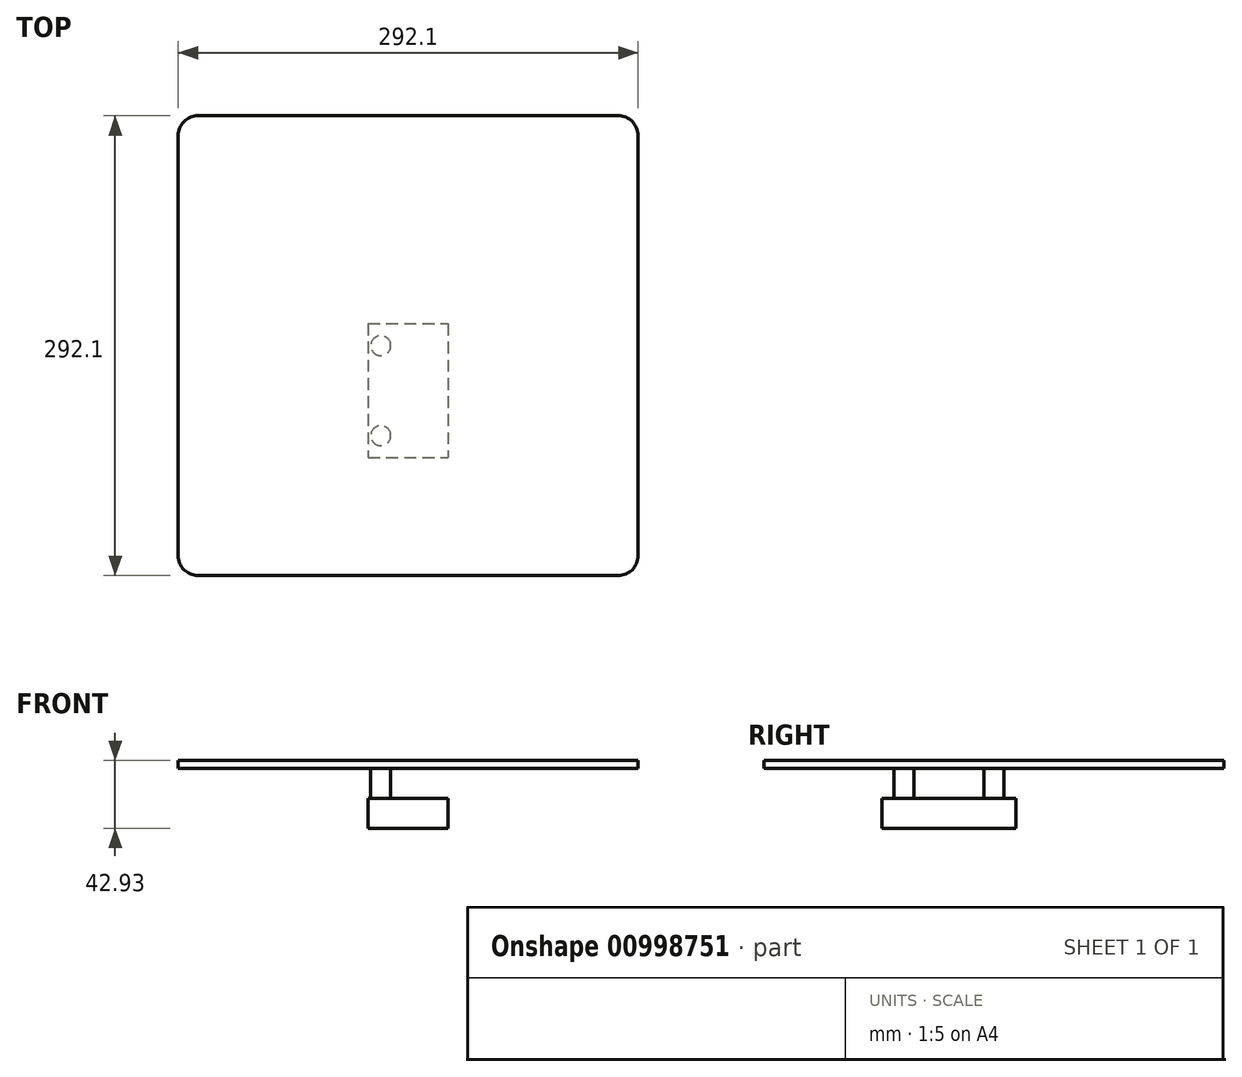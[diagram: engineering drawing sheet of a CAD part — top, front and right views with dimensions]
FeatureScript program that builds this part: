
annotation { "Feature Type Name" : "Feature", "Feature Type Description" : "" }
export const myFeature = defineFeature(function(context is Context, id is Id, definition is map)
    precondition{}
    {
        {
            var Q0;
            Q0=qCreatedBy(makeId("Top.planeOp"),FACE);
            var sketch = newSketch(context, id + "F0", { "sketchPlane" : qUnion([Q0])});
            skLineSegment(sketch, "E0.bottom", {"start": v(133.35, 146.05) * mm, "end": v(-133.35, 146.05) * mm});
            skLineSegment(sketch, "E0.top", {"start": v(133.35, -146.05) * mm, "end": v(-133.35, -146.05) * mm});
            skLineSegment(sketch, "E0.left", {"start": v(146.05, 133.35) * mm, "end": v(146.05, -133.35) * mm});
            skLineSegment(sketch, "E0.right", {"start": v(-146.05, 133.35) * mm, "end": v(-146.05, -133.35) * mm});
            skPoint(sketch, "E0.middle", {"position": v(0, 0) * mm});
            skPoint(sketch, "E1.visualSharp", {"position": v(-146.05, 146.05) * mm});
            skArc(sketch, "E1.filletArc", {"start": v(-133.35, 146.05) * mm, "mid": v(-142.33, 142.33) * mm, "end": v(-146.05, 133.35) * mm});
            skPoint(sketch, "E2.visualSharp", {"position": v(146.05, 146.05) * mm});
            skArc(sketch, "E2.filletArc", {"start": v(146.05, 133.35) * mm, "mid": v(142.33, 142.33) * mm, "end": v(133.35, 146.05) * mm});
            skPoint(sketch, "E3.visualSharp", {"position": v(146.05, -146.05) * mm});
            skArc(sketch, "E3.filletArc", {"start": v(133.35, -146.05) * mm, "mid": v(142.33, -142.33) * mm, "end": v(146.05, -133.35) * mm});
            skPoint(sketch, "E4.visualSharp", {"position": v(-146.05, -146.05) * mm});
            skArc(sketch, "E4.filletArc", {"start": v(-146.05, -133.35) * mm, "mid": v(-142.33, -142.33) * mm, "end": v(-133.35, -146.05) * mm});
            skSolve(sketch);
        }
        {
            var Q0;
            Q0=makeQuery(id+"F0.imprint","IMPRINT",FACE,{"disambiguationData":[TD([[makeQuery(id+"F0.imprint","IMPRINT",EDGE,{"derivedFrom":sQuery(id+"F0.wireOp",EDGE,"E0.bottom")}),1.0]])]});
            extrude(context, id + "F1", {"entities" : qUnion([Q0]), "depth" : 4.83 * mm, "offsetDistance" : 25.4 * mm});
        }
        {
            var Q0;
            Q0=qCreatedBy(makeId("Top.planeOp"),FACE);
            var sketch = newSketch(context, id + "F2", { "sketchPlane" : qUnion([Q0])});
            skCircle(sketch, "E5", {"center": v(-17.4, 0) * mm, "radius": 6.35 * mm});
            skCircle(sketch, "E6", {"center": v(-17.4, -57.15) * mm, "radius": 6.35 * mm});
            skCircle(sketch, "E7.MirrorC", {"center": v(17.4, 0) * mm, "radius": 6.35 * mm});
            skCircle(sketch, "E8.MirrorC", {"center": v(17.4, -57.15) * mm, "radius": 6.35 * mm});
            skSolve(sketch);
        }
        {
            var Q0;
            Q0=makeQuery(id+"F2.imprint","IMPRINT",FACE,{"disambiguationData":[TD([[makeQuery(id+"F2.imprint","IMPRINT",EDGE,{"derivedFrom":sQuery(id+"F2.wireOp",EDGE,"E6")}),1.0]])]});
            var Q1;
            Q1=makeQuery(id+"F2.imprint","IMPRINT",FACE,{"disambiguationData":[TD([[makeQuery(id+"F2.imprint","IMPRINT",EDGE,{"derivedFrom":sQuery(id+"F2.wireOp",EDGE,"E8.MirrorC")}),-1.0]])]});
            var Q2;
            Q2=makeQuery(id+"F2.imprint","IMPRINT",FACE,{"disambiguationData":[TD([[makeQuery(id+"F2.imprint","IMPRINT",EDGE,{"derivedFrom":sQuery(id+"F2.wireOp",EDGE,"E7.MirrorC")}),-1.0]])]});
            var Q3;
            Q3=makeQuery(id+"F2.imprint","IMPRINT",FACE,{"disambiguationData":[TD([[makeQuery(id+"F2.imprint","IMPRINT",EDGE,{"derivedFrom":sQuery(id+"F2.wireOp",EDGE,"E5")}),1.0]])]});
            extrude(context, id + "F3", {"entities" : qUnion([Q0, Q1, Q2, Q3]), "operationType" : NewBodyOperationType.ADD, "oppositeDirection" : true, "depth" : 19.05 * mm, "offsetDistance" : 25.4 * mm});
        }
        {
            var Q0;
            Q0=qCreatedBy(makeId("Top.planeOp"),FACE);
            cPlane(context, id + "F4", {"entities" : qUnion([Q0]), "cplaneType" : CPlaneType.OFFSET, "offset" : 19.05 * mm, "oppositeDirection" : true, "width" : 152.4 * mm, "height" : 152.4 * mm});
        }
        {
            var Q0;
            Q0=qCreatedBy(id+"F4.planeOp",FACE);
            var sketch = newSketch(context, id + "F5", { "sketchPlane" : qUnion([Q0])});
            skLineSegment(sketch, "E9.MirrorCS", {"start": v(-25.4, -71.12) * mm, "end": v(25.4, -71.12) * mm});
            skLineSegment(sketch, "E10.MirrorCS", {"start": v(25.4, 13.97) * mm, "end": v(25.4, -71.12) * mm});
            skLineSegment(sketch, "E11.MirrorCS", {"start": v(-25.4, 13.97) * mm, "end": v(-25.4, -71.12) * mm});
            skLineSegment(sketch, "E12.MirrorCS", {"start": v(-25.4, 13.97) * mm, "end": v(25.4, 13.97) * mm});
            skSolve(sketch);
        }
        {
            var Q0;
            Q0=makeQuery(id+"F5.imprint","IMPRINT",FACE,{"disambiguationData":[TD([[makeQuery(id+"F5.imprint","IMPRINT",EDGE,{"derivedFrom":sQuery(id+"F5.wireOp",EDGE,"E9.MirrorCS")}),1.0]])]});
            extrude(context, id + "F6", {"entities" : qUnion([Q0]), "operationType" : NewBodyOperationType.ADD, "oppositeDirection" : true, "depth" : 19.05 * mm, "offsetDistance" : 25.4 * mm});
        }
    });
